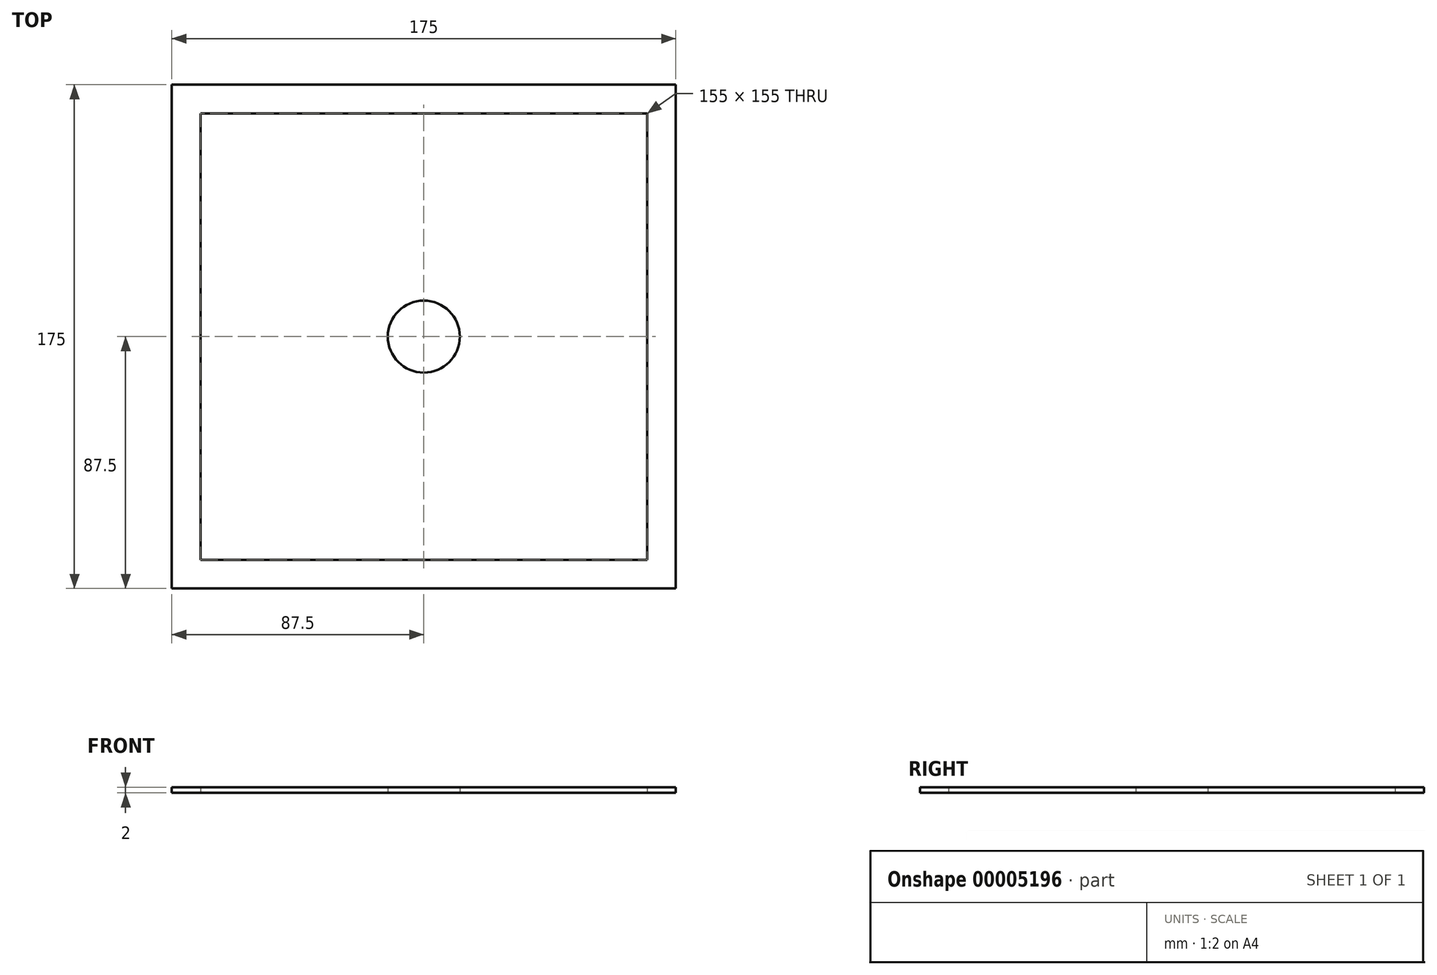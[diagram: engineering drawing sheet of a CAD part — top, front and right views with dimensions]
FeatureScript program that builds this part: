
annotation { "Feature Type Name" : "Feature", "Feature Type Description" : "" }
export const myFeature = defineFeature(function(context is Context, id is Id, definition is map)
    precondition{}
    {
        {
            var Q0;
            Q0=qCreatedBy(makeId("Top.planeOp"),FACE);
            var sketch = newSketch(context, id + "F0", { "sketchPlane" : qUnion([Q0])});
            skLineSegment(sketch, "E0.bottom", {"start": v(77.5, 77.5) * mm, "end": v(-77.5, 77.5) * mm});
            skLineSegment(sketch, "E0.top", {"start": v(77.5, -77.5) * mm, "end": v(-77.5, -77.5) * mm});
            skLineSegment(sketch, "E0.left", {"start": v(77.5, 77.5) * mm, "end": v(77.5, -77.5) * mm});
            skLineSegment(sketch, "E0.right", {"start": v(-77.5, 77.5) * mm, "end": v(-77.5, -77.5) * mm});
            skPoint(sketch, "E0.middle", {"position": v(0, 0) * mm});
            skLineSegment(sketch, "E1.bottom", {"start": v(87.5, 87.5) * mm, "end": v(-87.5, 87.5) * mm});
            skLineSegment(sketch, "E1.top", {"start": v(87.5, -87.5) * mm, "end": v(-87.5, -87.5) * mm});
            skLineSegment(sketch, "E1.left", {"start": v(87.5, 87.5) * mm, "end": v(87.5, -87.5) * mm});
            skLineSegment(sketch, "E1.right", {"start": v(-87.5, 87.5) * mm, "end": v(-87.5, -87.5) * mm});
            skCircle(sketch, "E2", {"center": v(0, 0) * mm, "radius": 12.5 * mm});
            skSolve(sketch);
        }
        {
            var Q0;
            Q0 = qSketchRegion(id + "F0", true);
            var Q1;
            Q1=makeQuery(id+"F0.imprint","IMPRINT",FACE,{"disambiguationData":[TD([[makeQuery(id+"F0.imprint","IMPRINT",EDGE,{"derivedFrom":sQuery(id+"F0.wireOp",EDGE,"E2")}),1.0]])]});
            extrude(context, id + "F1", {"entities" : qUnion([Q0, Q1]), "depth" : 2 * mm});
        }
    });
